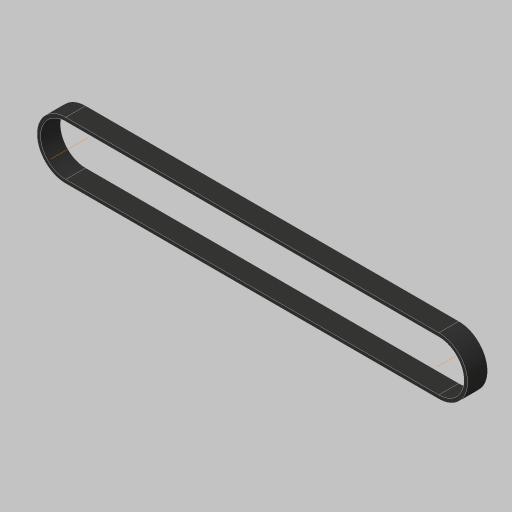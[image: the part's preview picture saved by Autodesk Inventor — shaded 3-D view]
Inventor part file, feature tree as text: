
AUTODESK INVENTOR PART (.ipt)
format: ipt  version: 2023.5 (Build 275446000, 446)  size: 162,304 bytes
history: native  units: in
note: dims shown in document units (in); Inventor stores cm internally (conversion verified against a paired STEP export)
features: sketch x3, extrude x1, other x1, projected_geometry x1
ambient origin geometry x8: Origin, YZ Plane, XZ Plane, XY Plane, X Axis, Y Axis, Z Axis, Center Point
bodies: Body1 (feature_tree)
feature tree (6):
  sketch  "Sketch2"  dims[d0=0.9023in d1=0.9023in]
  extrude  "Extrusion2"  Depth=0.9023in
  sketch  "Sketch5"  dims[d3=1.4174in d5=6.2598in d9=0.0787in d10=0.0598in d11=0.0299in d12=0.0219in d13=0.0219in d14=0.0059in d15=0.0059in d20=0.3346in d21=0.0in d22=0.0787in d23=0.0598in d24=0.0299in d25=0.0219in d26=0.0219in d27=0.0059in d28=0.0059in d29=0.0299in d30=0.0394in d31=0.0787in d32=0.0232in d34=0.0219in d35=0.0in d36=0.0in d37=0.0059in d38=0.0022in d39=0.0022in d40=0.0in d41=0.0in d42=0.0081in d43=0.0081in d44=0.0299in]
  other  "Work Axis1"
  sketch  "Sketch4"  dims[d2=1.4174in]
  projected_geometry  "Projected Loop1"
